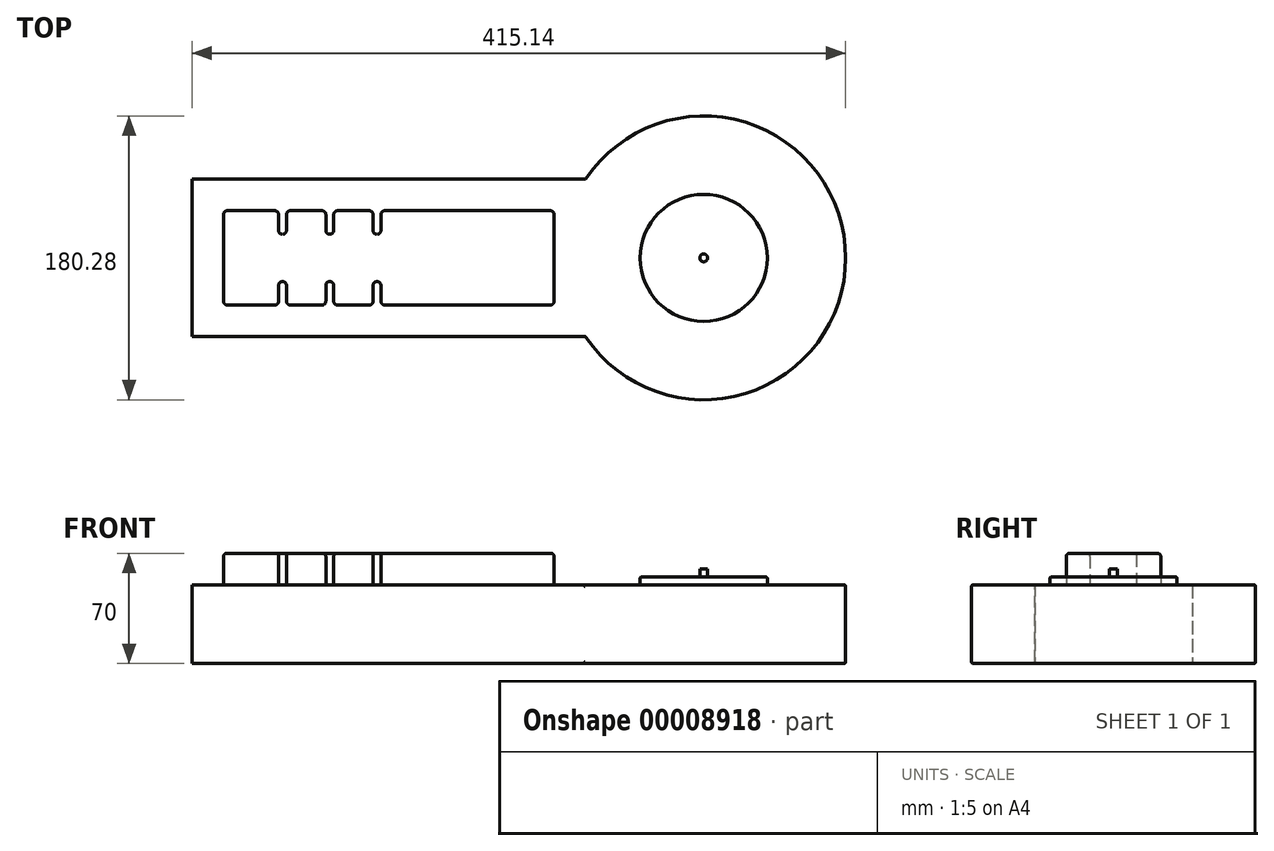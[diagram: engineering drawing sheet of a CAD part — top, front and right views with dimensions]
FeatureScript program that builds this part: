
annotation { "Feature Type Name" : "Feature", "Feature Type Description" : "" }
export const myFeature = defineFeature(function(context is Context, id is Id, definition is map)
    precondition{}
    {
        {
            var Q0;
            Q0=qCreatedBy(makeId("Top.planeOp"),FACE);
            var sketch = newSketch(context, id + "F0", { "sketchPlane" : qUnion([Q0])});
            skLineSegment(sketch, "E0.bottom", {"start": v(0, 0) * mm, "end": v(250, 0) * mm});
            skLineSegment(sketch, "E0.top", {"start": v(0, 100) * mm, "end": v(250, 100) * mm});
            skLineSegment(sketch, "E0.left", {"start": v(0, 0) * mm, "end": v(0, 100) * mm});
            skLineSegment(sketch, "E0.right", {"start": v(250, 0) * mm, "end": v(250, 100) * mm});
            skArc(sketch, "E1", {"start": v(250, 0) * mm, "mid": v(415.14, 50) * mm, "end": v(250, 100) * mm});
            skSolve(sketch);
        }
        {
            var Q0;
            Q0=makeQuery(id+"F0.imprint","IMPRINT",FACE,{"disambiguationData":[TD([[makeQuery(id+"F0.imprint","IMPRINT",EDGE,{"derivedFrom":sQuery(id+"F0.wireOp",EDGE,"E0.bottom")}),1.0]])]});
            var Q1;
            Q1=makeQuery(id+"F0.imprint","IMPRINT",FACE,{"disambiguationData":[TD([[makeQuery(id+"F0.imprint","IMPRINT",EDGE,{"derivedFrom":sQuery(id+"F0.wireOp",EDGE,"E0.right")}),-1.0]])]});
            extrude(context, id + "F1", {"entities" : qUnion([Q0, Q1]), "depth" : 50 * mm});
        }
        {
            var Q0;
            Q0=makeQuery(id+"F1.opExtrude","CAP_FACE",FACE,{"disambiguationData":[OSD([sQuery(id+"F0.wireOp",EDGE,"E0.bottom"),sQuery(id+"F0.wireOp",EDGE,"E0.top"),sQuery(id+"F0.wireOp",EDGE,"E0.left"),sQuery(id+"F0.wireOp",EDGE,"E1")])],"isStart":false});
            var sketch = newSketch(context, id + "F2", { "sketchPlane" : qUnion([Q0])});
            skLineSegment(sketch, "E2.bottom", {"start": v(20, 80) * mm, "end": v(230, 80) * mm});
            skLineSegment(sketch, "E2.top", {"start": v(20, 20) * mm, "end": v(230, 20) * mm});
            skLineSegment(sketch, "E2.left", {"start": v(20, 80) * mm, "end": v(20, 20) * mm});
            skLineSegment(sketch, "E2.right", {"start": v(230, 80) * mm, "end": v(230, 20) * mm});
            skLineSegment(sketch, "E3.bottom", {"start": v(55, 80) * mm, "end": v(60, 80) * mm});
            skLineSegment(sketch, "E3.top", {"start": v(55, 65) * mm, "end": v(60, 65) * mm});
            skLineSegment(sketch, "E3.left", {"start": v(55, 80) * mm, "end": v(55, 65) * mm});
            skLineSegment(sketch, "E3.right", {"start": v(60, 80) * mm, "end": v(60, 65) * mm});
            skLineSegment(sketch, "E4.bottom", {"start": v(85, 80) * mm, "end": v(90, 80) * mm});
            skLineSegment(sketch, "E4.top", {"start": v(85, 65) * mm, "end": v(90, 65) * mm});
            skLineSegment(sketch, "E4.left", {"start": v(85, 80) * mm, "end": v(85, 65) * mm});
            skLineSegment(sketch, "E4.right", {"start": v(90, 80) * mm, "end": v(90, 65) * mm});
            skLineSegment(sketch, "E5.bottom", {"start": v(115, 80) * mm, "end": v(120, 80) * mm});
            skLineSegment(sketch, "E5.top", {"start": v(115, 65) * mm, "end": v(120, 65) * mm});
            skLineSegment(sketch, "E5.left", {"start": v(115, 80) * mm, "end": v(115, 65) * mm});
            skLineSegment(sketch, "E5.right", {"start": v(120, 80) * mm, "end": v(120, 65) * mm});
            skLineSegment(sketch, "E6.bottom", {"start": v(55, 20) * mm, "end": v(60, 20) * mm});
            skLineSegment(sketch, "E6.top", {"start": v(55, 35) * mm, "end": v(60, 35) * mm});
            skLineSegment(sketch, "E6.left", {"start": v(55, 20) * mm, "end": v(55, 35) * mm});
            skLineSegment(sketch, "E6.right", {"start": v(60, 20) * mm, "end": v(60, 35) * mm});
            skLineSegment(sketch, "E7.bottom", {"start": v(85, 20) * mm, "end": v(90, 20) * mm});
            skLineSegment(sketch, "E7.top", {"start": v(85, 35) * mm, "end": v(90, 35) * mm});
            skLineSegment(sketch, "E7.left", {"start": v(85, 20) * mm, "end": v(85, 35) * mm});
            skLineSegment(sketch, "E7.right", {"start": v(90, 20) * mm, "end": v(90, 35) * mm});
            skLineSegment(sketch, "E8.bottom", {"start": v(115, 20) * mm, "end": v(120, 20) * mm});
            skLineSegment(sketch, "E8.top", {"start": v(115, 35) * mm, "end": v(120, 35) * mm});
            skLineSegment(sketch, "E8.left", {"start": v(115, 20) * mm, "end": v(115, 35) * mm});
            skLineSegment(sketch, "E8.right", {"start": v(120, 20) * mm, "end": v(120, 35) * mm});
            skSolve(sketch);
        }
        {
            var Q0;
            {var subQ20=sQuery(id+"F2.wireOp",EDGE,"E2.left");Q0=makeQuery(id+"F2.imprint","IMPRINT",FACE,{"disambiguationData":[TD([[makeQuery(id+"F2.imprint","IMPRINT",EDGE,{"derivedFrom":subQ20}),1.0]])]});}
            extrude(context, id + "F3", {"entities" : qUnion([Q0]), "operationType" : NewBodyOperationType.ADD, "depth" : 20 * mm});
        }
        {
            var Q0;
            Q0=makeQuery(id+"F1.opExtrude","CAP_FACE",FACE,{"disambiguationData":[OSD([sQuery(id+"F0.wireOp",EDGE,"E0.bottom"),sQuery(id+"F0.wireOp",EDGE,"E0.top"),sQuery(id+"F0.wireOp",EDGE,"E0.left"),sQuery(id+"F0.wireOp",EDGE,"E1")])],"isStart":false});
            var sketch = newSketch(context, id + "F4", { "sketchPlane" : qUnion([Q0])});
            skCircle(sketch, "E9", {"center": v(325, 50) * mm, "radius": 40.38 * mm});
            skSolve(sketch);
        }
        {
            var Q0;
            Q0 = qSketchRegion(id + "F4", true);
            extrude(context, id + "F5", {"entities" : qUnion([Q0]), "operationType" : NewBodyOperationType.ADD, "depth" : 5 * mm});
        }
        {
            var Q0;
            Q0=makeQuery(id+"F5.opExtrude","CAP_FACE",FACE,{"disambiguationData":[OSD([sQuery(id+"F4.wireOp",EDGE,"E9")])],"isStart":false});
            var sketch = newSketch(context, id + "F6", { "sketchPlane" : qUnion([Q0])});
            skCircle(sketch, "E10", {"center": v(325, 50) * mm, "radius": 2.5 * mm});
            skSolve(sketch);
        }
        {
            var Q0;
            Q0=makeQuery(id+"F6.imprint","IMPRINT",FACE,{"disambiguationData":[TD([[makeQuery(id+"F6.imprint","IMPRINT",EDGE,{"derivedFrom":sQuery(id+"F6.wireOp",EDGE,"E10")}),1.0]])]});
            extrude(context, id + "F7", {"entities" : qUnion([Q0]), "operationType" : NewBodyOperationType.ADD, "depth" : 5 * mm});
        }
        {
            var Q0;
            Q0=makeQuery(id+"F1.opExtrude","SWEPT_FACE",FACE,{"disambiguationData":[OSD([sQuery(id+"F0.wireOp",EDGE,"E1")])]});
            var Q1;
            Q1=makeQuery(id+"F5.opExtrude","CAP_EDGE",EDGE,{"disambiguationData":[OSD([sQuery(id+"F4.wireOp",EDGE,"E9")])],"isStart":false});
            var Q2;
            Q2=makeQuery(id+"F5.opExtrude","CAP_EDGE",EDGE,{"disambiguationData":[OSD([sQuery(id+"F4.wireOp",EDGE,"E9")])],"isStart":true});
            fillet(context, id + "F8", {"entities" : qUnion([Q0, Q1, Q2]), "radius" : 1 * mm, "tangentPropagation" : true, "allowEdgeOverflow" : false});
        }
        {
            var Q0;
            Q0=makeQuery(id+"F3.opExtrude","SWEPT_EDGE",EDGE,{"disambiguationData":[OSD([sQuery(id+"F2.wireOp",EDGE,"E6.top"),sQuery(id+"F2.wireOp",EDGE,"E6.left")])]});
            var Q1;
            Q1=makeQuery(id+"F3.opExtrude","SWEPT_EDGE",EDGE,{"disambiguationData":[OSD([sQuery(id+"F2.wireOp",EDGE,"E2.top"),sQuery(id+"F2.wireOp",EDGE,"E6.bottom"),sQuery(id+"F2.wireOp",EDGE,"E6.left")])]});
            var Q2;
            Q2=makeQuery(id+"F3.opExtrude","SWEPT_EDGE",EDGE,{"disambiguationData":[OSD([sQuery(id+"F2.wireOp",EDGE,"E6.top"),sQuery(id+"F2.wireOp",EDGE,"E6.right")])]});
            var Q3;
            Q3=makeQuery(id+"F3.opExtrude","SWEPT_EDGE",EDGE,{"disambiguationData":[OSD([sQuery(id+"F2.wireOp",EDGE,"E2.top"),sQuery(id+"F2.wireOp",EDGE,"E6.bottom"),sQuery(id+"F2.wireOp",EDGE,"E6.right")])]});
            var Q4;
            Q4=makeQuery(id+"F3.opExtrude","SWEPT_EDGE",EDGE,{"disambiguationData":[OSD([sQuery(id+"F2.wireOp",EDGE,"E2.top"),sQuery(id+"F2.wireOp",EDGE,"E7.bottom"),sQuery(id+"F2.wireOp",EDGE,"E7.left")])]});
            var Q5;
            Q5=makeQuery(id+"F3.opExtrude","SWEPT_EDGE",EDGE,{"disambiguationData":[OSD([sQuery(id+"F2.wireOp",EDGE,"E7.top"),sQuery(id+"F2.wireOp",EDGE,"E7.right")])]});
            var Q6;
            Q6=makeQuery(id+"F3.opExtrude","SWEPT_EDGE",EDGE,{"disambiguationData":[OSD([sQuery(id+"F2.wireOp",EDGE,"E2.top"),sQuery(id+"F2.wireOp",EDGE,"E7.bottom"),sQuery(id+"F2.wireOp",EDGE,"E7.right")])]});
            var Q7;
            Q7=makeQuery(id+"F3.opExtrude","SWEPT_EDGE",EDGE,{"disambiguationData":[OSD([sQuery(id+"F2.wireOp",EDGE,"E2.top"),sQuery(id+"F2.wireOp",EDGE,"E8.bottom"),sQuery(id+"F2.wireOp",EDGE,"E8.left")])]});
            var Q8;
            Q8=makeQuery(id+"F3.opExtrude","SWEPT_EDGE",EDGE,{"disambiguationData":[OSD([sQuery(id+"F2.wireOp",EDGE,"E8.top"),sQuery(id+"F2.wireOp",EDGE,"E8.right")])]});
            var Q9;
            Q9=makeQuery(id+"F3.opExtrude","SWEPT_EDGE",EDGE,{"disambiguationData":[OSD([sQuery(id+"F2.wireOp",EDGE,"E2.top"),sQuery(id+"F2.wireOp",EDGE,"E8.bottom"),sQuery(id+"F2.wireOp",EDGE,"E8.right")])]});
            var Q10;
            Q10=makeQuery(id+"F3.opExtrude","SWEPT_EDGE",EDGE,{"disambiguationData":[OSD([sQuery(id+"F2.wireOp",EDGE,"E7.top"),sQuery(id+"F2.wireOp",EDGE,"E7.left")])]});
            var Q11;
            Q11=makeQuery(id+"F3.opExtrude","SWEPT_EDGE",EDGE,{"disambiguationData":[OSD([sQuery(id+"F2.wireOp",EDGE,"E8.top"),sQuery(id+"F2.wireOp",EDGE,"E8.left")])]});
            var Q12;
            Q12=makeQuery(id+"F3.opExtrude","SWEPT_EDGE",EDGE,{"disambiguationData":[OSD([sQuery(id+"F2.wireOp",EDGE,"E3.top"),sQuery(id+"F2.wireOp",EDGE,"E3.left")])]});
            var Q13;
            Q13=makeQuery(id+"F3.opExtrude","SWEPT_EDGE",EDGE,{"disambiguationData":[OSD([sQuery(id+"F2.wireOp",EDGE,"E2.bottom"),sQuery(id+"F2.wireOp",EDGE,"E3.bottom"),sQuery(id+"F2.wireOp",EDGE,"E3.left")])]});
            var Q14;
            Q14=makeQuery(id+"F3.opExtrude","SWEPT_EDGE",EDGE,{"disambiguationData":[OSD([sQuery(id+"F2.wireOp",EDGE,"E4.top"),sQuery(id+"F2.wireOp",EDGE,"E4.left")])]});
            var Q15;
            Q15=makeQuery(id+"F3.opExtrude","SWEPT_EDGE",EDGE,{"disambiguationData":[OSD([sQuery(id+"F2.wireOp",EDGE,"E2.bottom"),sQuery(id+"F2.wireOp",EDGE,"E4.bottom"),sQuery(id+"F2.wireOp",EDGE,"E4.left")])]});
            var Q16;
            Q16=makeQuery(id+"F3.opExtrude","SWEPT_EDGE",EDGE,{"disambiguationData":[OSD([sQuery(id+"F2.wireOp",EDGE,"E5.top"),sQuery(id+"F2.wireOp",EDGE,"E5.left")])]});
            var Q17;
            Q17=makeQuery(id+"F3.opExtrude","SWEPT_EDGE",EDGE,{"disambiguationData":[OSD([sQuery(id+"F2.wireOp",EDGE,"E2.bottom"),sQuery(id+"F2.wireOp",EDGE,"E5.bottom"),sQuery(id+"F2.wireOp",EDGE,"E5.left")])]});
            var Q18;
            Q18=makeQuery(id+"F3.opExtrude","SWEPT_EDGE",EDGE,{"disambiguationData":[OSD([sQuery(id+"F2.wireOp",EDGE,"E3.top"),sQuery(id+"F2.wireOp",EDGE,"E3.right")])]});
            var Q19;
            Q19=makeQuery(id+"F3.opExtrude","SWEPT_EDGE",EDGE,{"disambiguationData":[OSD([sQuery(id+"F2.wireOp",EDGE,"E2.bottom"),sQuery(id+"F2.wireOp",EDGE,"E3.bottom"),sQuery(id+"F2.wireOp",EDGE,"E3.right")])]});
            var Q20;
            Q20=makeQuery(id+"F3.opExtrude","SWEPT_EDGE",EDGE,{"disambiguationData":[OSD([sQuery(id+"F2.wireOp",EDGE,"E4.top"),sQuery(id+"F2.wireOp",EDGE,"E4.right")])]});
            var Q21;
            Q21=makeQuery(id+"F3.opExtrude","SWEPT_EDGE",EDGE,{"disambiguationData":[OSD([sQuery(id+"F2.wireOp",EDGE,"E2.bottom"),sQuery(id+"F2.wireOp",EDGE,"E4.bottom"),sQuery(id+"F2.wireOp",EDGE,"E4.right")])]});
            var Q22;
            Q22=makeQuery(id+"F3.opExtrude","SWEPT_EDGE",EDGE,{"disambiguationData":[OSD([sQuery(id+"F2.wireOp",EDGE,"E5.top"),sQuery(id+"F2.wireOp",EDGE,"E5.right")])]});
            var Q23;
            Q23=makeQuery(id+"F3.opExtrude","SWEPT_EDGE",EDGE,{"disambiguationData":[OSD([sQuery(id+"F2.wireOp",EDGE,"E2.bottom"),sQuery(id+"F2.wireOp",EDGE,"E5.bottom"),sQuery(id+"F2.wireOp",EDGE,"E5.right")])]});
            var Q24;
            Q24=makeQuery(id+"F3.opExtrude","SWEPT_EDGE",EDGE,{"disambiguationData":[OSD([sQuery(id+"F2.wireOp",EDGE,"E2.bottom"),sQuery(id+"F2.wireOp",EDGE,"E2.left")])]});
            var Q25;
            Q25=makeQuery(id+"F3.opExtrude","SWEPT_EDGE",EDGE,{"disambiguationData":[OSD([sQuery(id+"F2.wireOp",EDGE,"E2.top"),sQuery(id+"F2.wireOp",EDGE,"E2.left")])]});
            var Q26;
            Q26=makeQuery(id+"F3.opExtrude","SWEPT_EDGE",EDGE,{"disambiguationData":[OSD([sQuery(id+"F2.wireOp",EDGE,"E2.bottom"),sQuery(id+"F2.wireOp",EDGE,"E2.right")])]});
            var Q27;
            Q27=makeQuery(id+"F3.opExtrude","SWEPT_EDGE",EDGE,{"disambiguationData":[OSD([sQuery(id+"F2.wireOp",EDGE,"E2.top"),sQuery(id+"F2.wireOp",EDGE,"E2.right")])]});
            fillet(context, id + "F9", {"entities" : qUnion([Q0, Q1, Q2, Q3, Q4, Q5, Q6, Q7, Q8, Q9, Q10, Q11, Q12, Q13, Q14, Q15, Q16, Q17, Q18, Q19, Q20, Q21, Q22, Q23, Q24, Q25, Q26, Q27]), "radius" : 2.5 * mm, "tangentPropagation" : true, "allowEdgeOverflow" : false});
        }
        {
            var Q0;
            {var subQ0=sQuery(id+"F2.wireOp",EDGE,"E2.bottom");Q0=makeQuery(id+"F3.opExtrude","CAP_EDGE",EDGE,{"disambiguationData":[OSD([subQ0]),TDD([makeQuery(id+"F2.imprint","IMPRINT",EDGE,{"disambiguationData":[TD([[makeQuery(id+"F2.imprint","INTERSECT",VERTEX,{"derivedFrom":[subQ0,sQuery(id+"F2.wireOp",EDGE,"E2.right")]}),1.0]])],"derivedFrom":subQ0})])],"isStart":false});}
            var Q1;
            Q1=makeQuery(id+"F3.opExtrude","CAP_EDGE",EDGE,{"disambiguationData":[OSD([sQuery(id+"F2.wireOp",EDGE,"E2.right")])],"isStart":false});
            fillet(context, id + "F10", {"entities" : qUnion([Q0, Q1]), "radius" : 2 * mm, "tangentPropagation" : true, "allowEdgeOverflow" : false});
        }
    });
